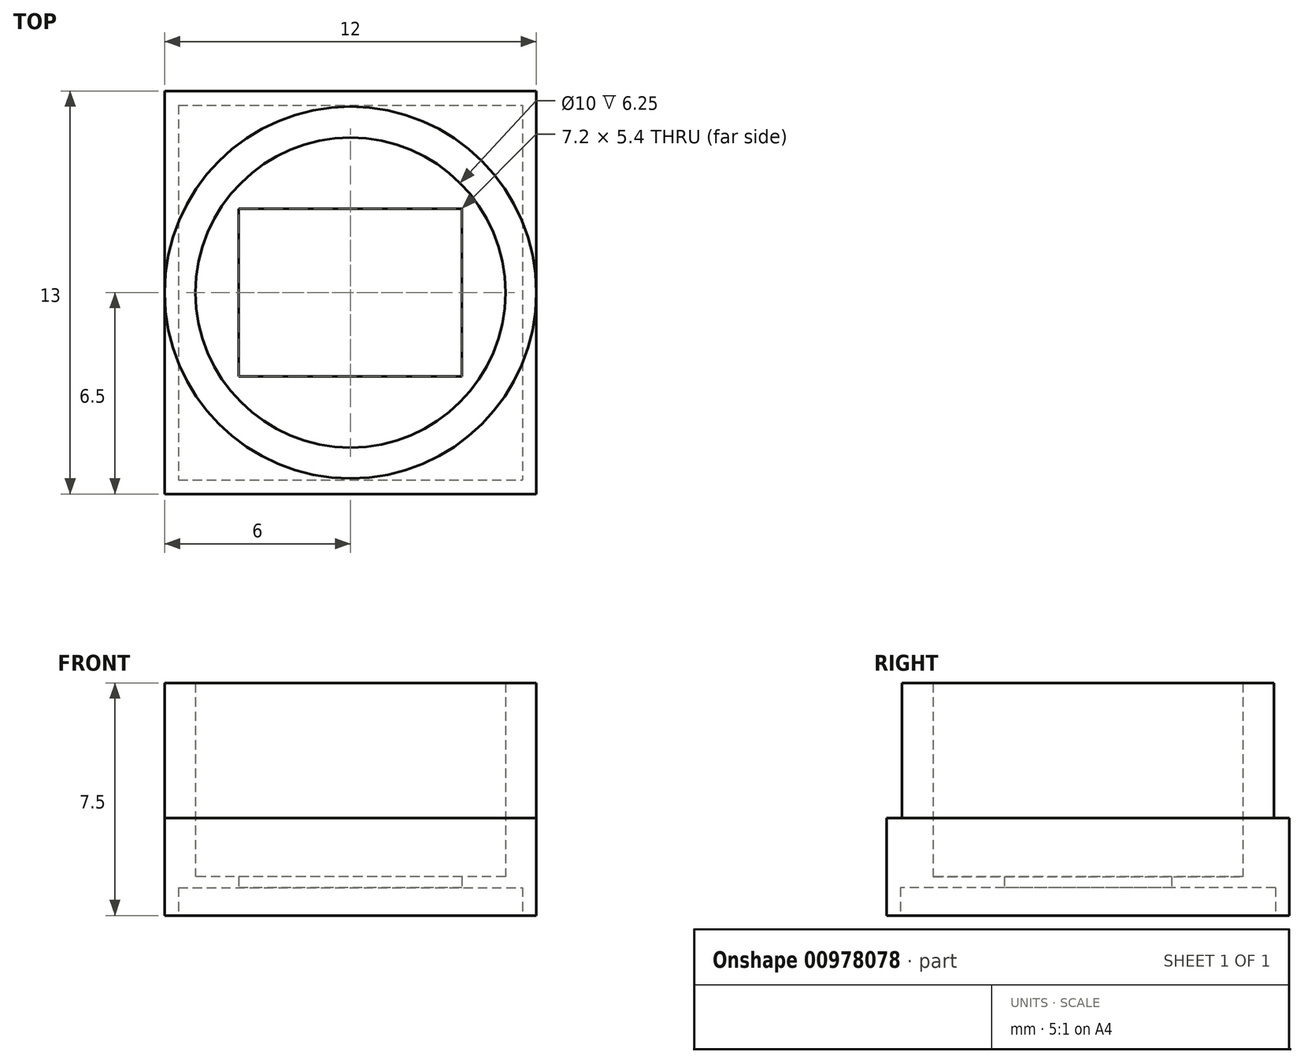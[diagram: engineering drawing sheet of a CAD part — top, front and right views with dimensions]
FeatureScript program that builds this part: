
annotation { "Feature Type Name" : "Feature", "Feature Type Description" : "" }
export const myFeature = defineFeature(function(context is Context, id is Id, definition is map)
    precondition{}
    {
        {
            var Q0;
            Q0=qCreatedBy(makeId("Top.planeOp"),FACE);
            var sketch = newSketch(context, id + "F0", { "sketchPlane" : qUnion([Q0])});
            skLineSegment(sketch, "E0.bottom", {"start": v(-6, 6.5) * mm, "end": v(6, 6.5) * mm});
            skLineSegment(sketch, "E0.top", {"start": v(-6, -6.5) * mm, "end": v(6, -6.5) * mm});
            skLineSegment(sketch, "E0.left", {"start": v(-6, 6.5) * mm, "end": v(-6, -6.5) * mm});
            skLineSegment(sketch, "E0.right", {"start": v(6, 6.5) * mm, "end": v(6, -6.5) * mm});
            skPoint(sketch, "E0.middle", {"position": v(0, 0) * mm});
            skLineSegment(sketch, "E1.bottom", {"start": v(-5.55, 6.05) * mm, "end": v(5.55, 6.05) * mm});
            skLineSegment(sketch, "E1.top", {"start": v(-5.55, -6.05) * mm, "end": v(5.55, -6.05) * mm});
            skLineSegment(sketch, "E1.left", {"start": v(-5.55, 6.05) * mm, "end": v(-5.55, -6.05) * mm});
            skLineSegment(sketch, "E1.right", {"start": v(5.55, 6.05) * mm, "end": v(5.55, -6.05) * mm});
            skLineSegment(sketch, "E2.bottom", {"start": v(3.6, 2.7) * mm, "end": v(-3.6, 2.7) * mm});
            skLineSegment(sketch, "E2.top", {"start": v(3.6, -2.7) * mm, "end": v(-3.6, -2.7) * mm});
            skLineSegment(sketch, "E2.left", {"start": v(3.6, 2.7) * mm, "end": v(3.6, -2.7) * mm});
            skLineSegment(sketch, "E2.right", {"start": v(-3.6, 2.7) * mm, "end": v(-3.6, -2.7) * mm});
            skSolve(sketch);
        }
        {
            var Q0;
            Q0=makeQuery(id+"F0.imprint","IMPRINT",FACE,{"disambiguationData":[TD([[makeQuery(id+"F0.imprint","IMPRINT",EDGE,{"derivedFrom":sQuery(id+"F0.wireOp",EDGE,"E0.bottom")}),-1.0]])]});
            var Q1;
            Q1=makeQuery(id+"F0.imprint","IMPRINT",FACE,{"disambiguationData":[TD([[makeQuery(id+"F0.imprint","IMPRINT",EDGE,{"derivedFrom":sQuery(id+"F0.wireOp",EDGE,"E1.bottom")}),-1.0]])]});
            extrude(context, id + "F1", {"entities" : qUnion([Q0, Q1]), "depth" : 3.15 * mm, "offsetDistance" : 25 * mm});
        }
        {
            var Q0;
            Q0=makeQuery(id+"F0.imprint","IMPRINT",FACE,{"disambiguationData":[TD([[makeQuery(id+"F0.imprint","IMPRINT",EDGE,{"derivedFrom":sQuery(id+"F0.wireOp",EDGE,"E1.bottom")}),-1.0]])]});
            extrude(context, id + "F2", {"entities" : qUnion([Q0]), "operationType" : NewBodyOperationType.REMOVE, "depth" : 0.9 * mm, "offsetDistance" : 25 * mm});
        }
        {
            var Q0;
            Q0=makeQuery(id+"F1.opExtrude","CAP_FACE",FACE,{"disambiguationData":[OSD([sQuery(id+"F0.wireOp",EDGE,"E0.bottom"),sQuery(id+"F0.wireOp",EDGE,"E0.top"),sQuery(id+"F0.wireOp",EDGE,"E0.left"),sQuery(id+"F0.wireOp",EDGE,"E0.right")])],"isStart":false});
            var sketch = newSketch(context, id + "F3", { "sketchPlane" : qUnion([Q0])});
            skCircle(sketch, "E3", {"center": v(0, 0) * mm, "radius": 6 * mm});
            skCircle(sketch, "E4", {"center": v(0, 0) * mm, "radius": 5 * mm});
            skSolve(sketch);
        }
        {
            var Q0;
            Q0=makeQuery(id+"F3.imprint","IMPRINT",FACE,{"disambiguationData":[TD([[makeQuery(id+"F3.imprint","IMPRINT",EDGE,{"derivedFrom":sQuery(id+"F3.wireOp",EDGE,"E3")}),1.0]])]});
            extrude(context, id + "F4", {"entities" : qUnion([Q0]), "operationType" : NewBodyOperationType.ADD, "depth" : 4.35 * mm, "offsetDistance" : 25 * mm});
        }
        {
            var Q0;
            {var subQ0=sQuery(id+"F0.wireOp",EDGE,"E2.right");var subQ1=sQuery(id+"F0.wireOp",EDGE,"E2.left");var subQ2=sQuery(id+"F0.wireOp",EDGE,"E2.top");var subQ3=sQuery(id+"F0.wireOp",EDGE,"E2.bottom");Q0=makeQuery(id+"F4.boolean.opBoolean","SPLIT",FACE,{"disambiguationData":[TD([makeQuery(id+"F1.opExtrude","SWEPT_FACE",FACE,{"disambiguationData":[OSD([subQ3])]})])],"derivedFrom":makeQuery(id+"F1.opExtrude","CAP_FACE",FACE,{"disambiguationData":[OSD([sQuery(id+"F0.wireOp",EDGE,"E0.bottom"),sQuery(id+"F0.wireOp",EDGE,"E0.top"),sQuery(id+"F0.wireOp",EDGE,"E0.left"),sQuery(id+"F0.wireOp",EDGE,"E0.right"),subQ3,subQ2,subQ1,subQ0])],"isStart":false})});}
            extrude(context, id + "F5", {"entities" : qUnion([Q0]), "operationType" : NewBodyOperationType.REMOVE, "oppositeDirection" : true, "depth" : 1.9 * mm, "offsetDistance" : 25 * mm});
        }
    });
